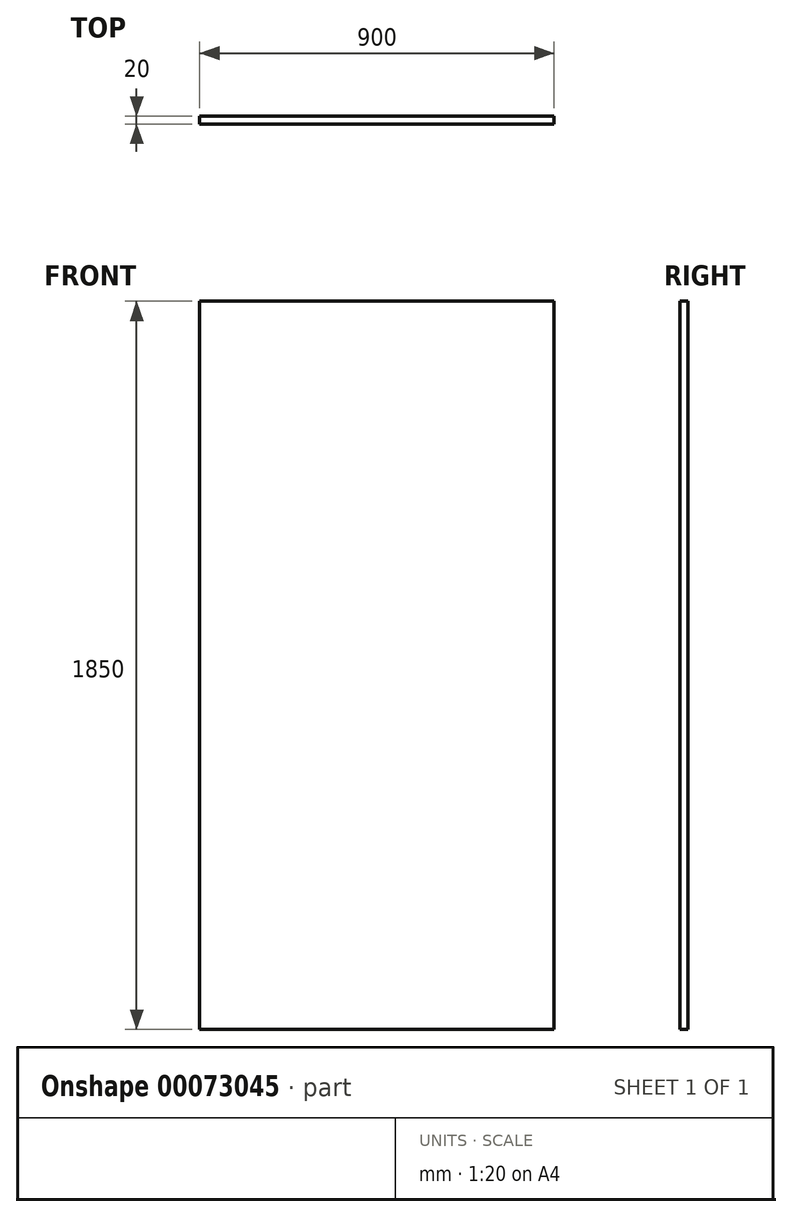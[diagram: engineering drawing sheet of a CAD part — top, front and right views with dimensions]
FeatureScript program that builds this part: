
annotation { "Feature Type Name" : "Feature", "Feature Type Description" : "" }
export const myFeature = defineFeature(function(context is Context, id is Id, definition is map)
    precondition{}
    {
        {
            var Q0;
            Q0=qCreatedBy(makeId("Top.planeOp"),FACE);
            var sketch = newSketch(context, id + "F0", { "sketchPlane" : qUnion([Q0])});
            skLineSegment(sketch, "E0.bottom", {"start": v(0, 0) * mm, "end": v(900, 0) * mm});
            skLineSegment(sketch, "E0.top", {"start": v(0, -20) * mm, "end": v(900, -20) * mm});
            skLineSegment(sketch, "E0.left", {"start": v(0, 0) * mm, "end": v(0, -20) * mm});
            skLineSegment(sketch, "E0.right", {"start": v(900, 0) * mm, "end": v(900, -20) * mm});
            skSolve(sketch);
        }
        {
            var Q0;
            Q0=makeQuery(id+"F0.imprint","IMPRINT",FACE,{"disambiguationData":[TD([[makeQuery(id+"F0.imprint","IMPRINT",EDGE,{"derivedFrom":sQuery(id+"F0.wireOp",EDGE,"E0.bottom")}),-1.0]])]});
            extrude(context, id + "F1", {"entities" : qUnion([Q0]), "depth" : 1850 * mm});
        }
    });
